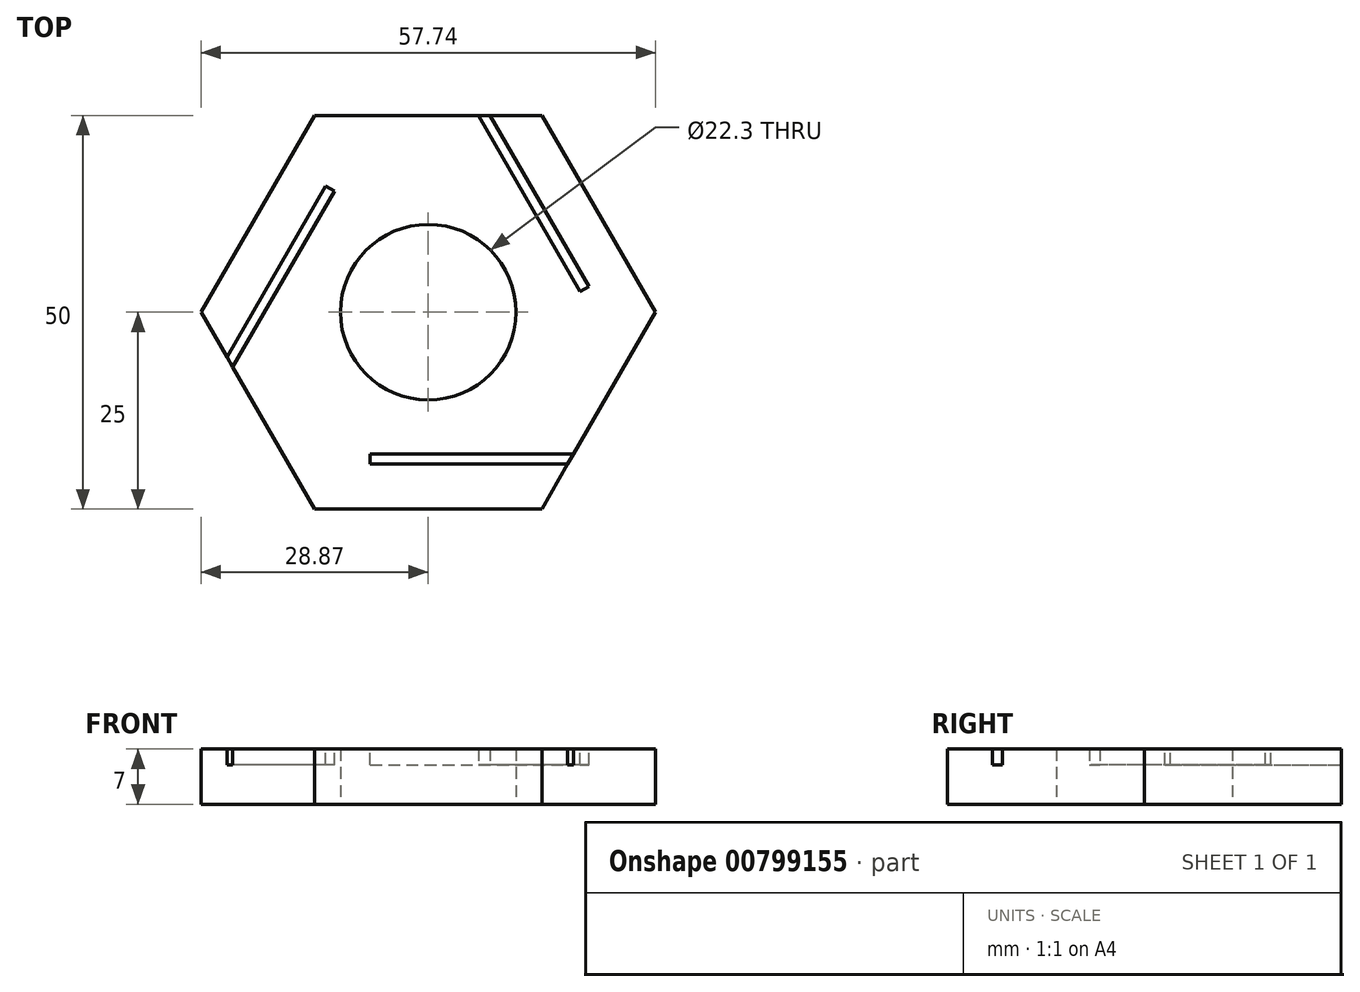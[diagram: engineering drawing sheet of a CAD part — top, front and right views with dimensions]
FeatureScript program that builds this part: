
annotation { "Feature Type Name" : "Feature", "Feature Type Description" : "" }
export const myFeature = defineFeature(function(context is Context, id is Id, definition is map)
    precondition{}
    {
        {
            var Q0;
            Q0=qCreatedBy(makeId("Top.planeOp"),FACE);
            var sketch = newSketch(context, id + "F0", { "sketchPlane" : qUnion([Q0])});
            skCircle(sketch, "E0.cCircle", {"center": v(0, 0) * mm, "radius": 25 * mm, "construction": true});
            skLineSegment(sketch, "E0.0", {"start": v(-14.43, 25) * mm, "end": v(14.43, 25) * mm});
            skLineSegment(sketch, "E0.1", {"start": v(14.43, 25) * mm, "end": v(28.87, 0) * mm});
            skLineSegment(sketch, "E0.2", {"start": v(28.87, 0) * mm, "end": v(14.43, -25) * mm});
            skLineSegment(sketch, "E0.3", {"start": v(14.43, -25) * mm, "end": v(-14.43, -25) * mm});
            skLineSegment(sketch, "E0.4", {"start": v(-14.43, -25) * mm, "end": v(-28.87, 0) * mm});
            skLineSegment(sketch, "E0.5", {"start": v(-28.87, 0) * mm, "end": v(-14.43, 25) * mm});
            skPoint(sketch, "E0.0.midPoint", {"position": v(0, 25) * mm});
            skCircle(sketch, "E1", {"center": v(0, 0) * mm, "radius": 11.15 * mm});
            skSolve(sketch);
        }
        {
            var Q0;
            Q0=makeQuery(id+"F0.imprint","IMPRINT",FACE,{"disambiguationData":[TD([[makeQuery(id+"F0.imprint","IMPRINT",EDGE,{"derivedFrom":sQuery(id+"F0.wireOp",EDGE,"E0.0")}),-1.0]])]});
            var Q1;
            Q1 = qSketchRegion(id + "F0", true);
            extrude(context, id + "F1", {"entities" : qUnion([Q0, Q1]), "depth" : 7 * mm, "offsetDistance" : 25 * mm});
        }
        {
            var Q0;
            Q0=makeQuery(id+"F1.opExtrude","CAP_FACE",FACE,{"disambiguationData":[OSD([sQuery(id+"F0.wireOp",EDGE,"E0.0"),sQuery(id+"F0.wireOp",EDGE,"E0.1"),sQuery(id+"F0.wireOp",EDGE,"E0.2"),sQuery(id+"F0.wireOp",EDGE,"E0.3"),sQuery(id+"F0.wireOp",EDGE,"E0.4"),sQuery(id+"F0.wireOp",EDGE,"E0.5"),sQuery(id+"F0.wireOp",EDGE,"E1")])],"isStart":false});
            var sketch = newSketch(context, id + "F2", { "sketchPlane" : qUnion([Q0])});
            skLineSegment(sketch, "E2.bottom", {"start": v(-7.37, -18) * mm, "end": v(33.87, -18) * mm});
            skLineSegment(sketch, "E2.top", {"start": v(-7.37, -19.31) * mm, "end": v(33.87, -19.31) * mm});
            skLineSegment(sketch, "E2.left", {"start": v(-7.37, -18) * mm, "end": v(-7.37, -19.31) * mm});
            skLineSegment(sketch, "E2.right", {"start": v(33.87, -18) * mm, "end": v(33.87, -19.31) * mm});
            skLineSegment(sketch, "E3.1.0", {"start": v(19.28, 2.62) * mm, "end": v(20.41, 3.27) * mm});
            skLineSegment(sketch, "E3.1.1", {"start": v(19.28, 2.62) * mm, "end": v(-1.34, 38.34) * mm});
            skLineSegment(sketch, "E3.1.2", {"start": v(20.41, 3.27) * mm, "end": v(-0.2, 38.99) * mm});
            skLineSegment(sketch, "E3.1.3", {"start": v(-1.34, 38.34) * mm, "end": v(-0.2, 38.99) * mm});
            skLineSegment(sketch, "E3.2.0", {"start": v(-11.9, 15.39) * mm, "end": v(-13.04, 16.04) * mm});
            skLineSegment(sketch, "E3.2.1", {"start": v(-11.9, 15.39) * mm, "end": v(-32.53, -20.33) * mm});
            skLineSegment(sketch, "E3.2.2", {"start": v(-13.04, 16.04) * mm, "end": v(-33.66, -19.68) * mm});
            skLineSegment(sketch, "E3.2.3", {"start": v(-32.53, -20.33) * mm, "end": v(-33.66, -19.68) * mm});
            skPoint(sketch, "E3.center", {"position": v(0, 0) * mm});
            skSolve(sketch);
        }
        {
            var Q0;
            Q0 = qSketchRegion(id + "F2", true);
            extrude(context, id + "F3", {"entities" : qUnion([Q0]), "operationType" : NewBodyOperationType.REMOVE, "oppositeDirection" : true, "depth" : 2 * mm, "offsetDistance" : 25 * mm});
        }
    });
